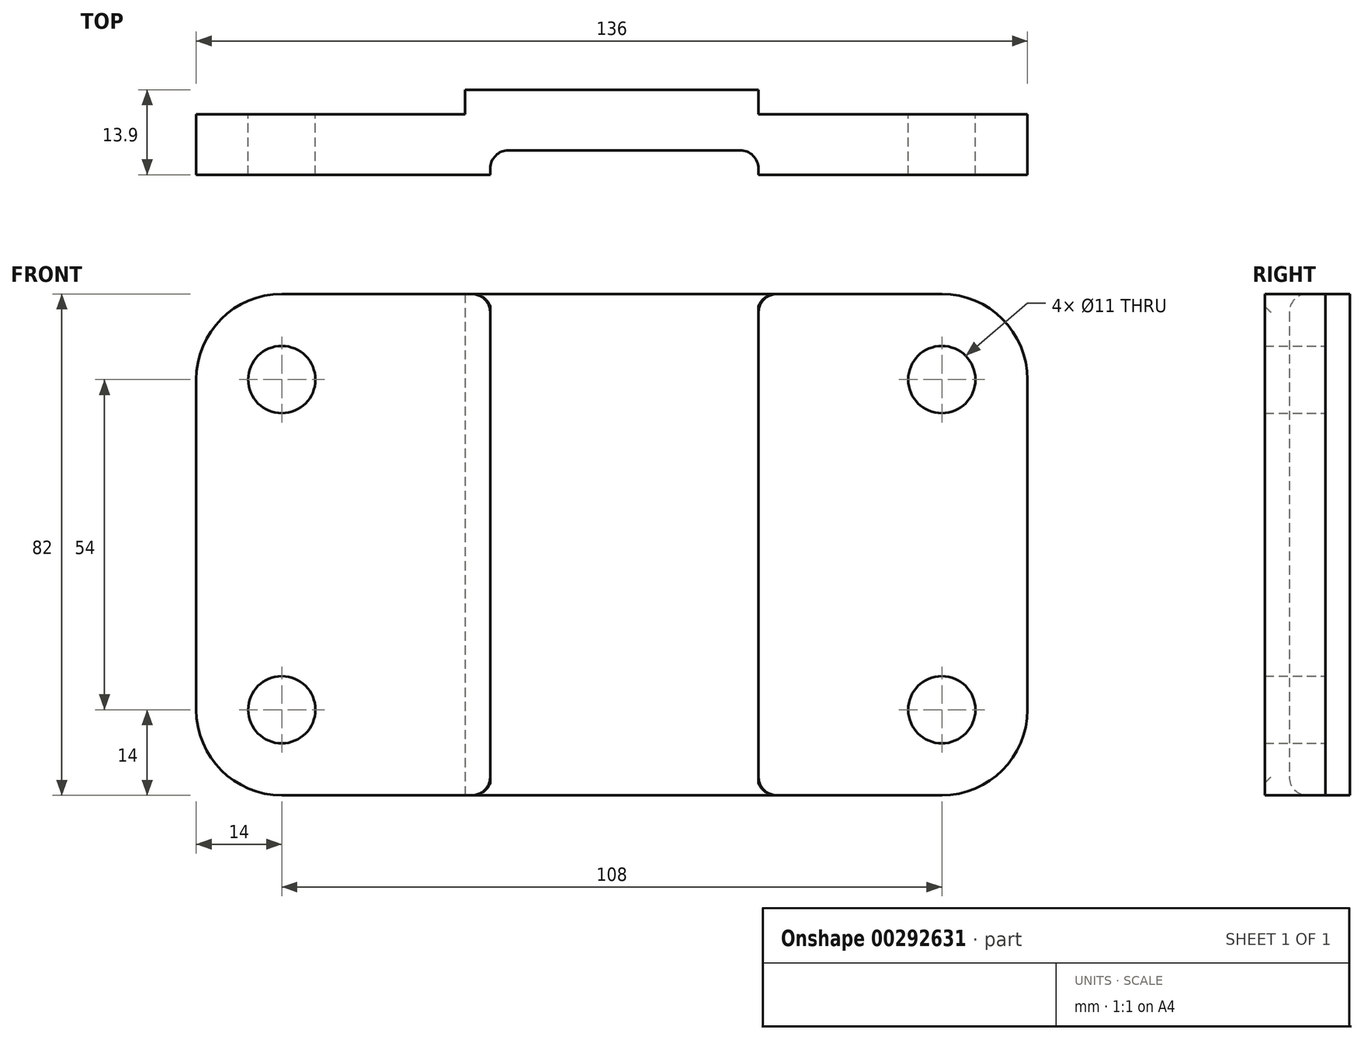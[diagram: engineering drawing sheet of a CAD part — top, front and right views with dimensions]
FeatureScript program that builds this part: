
annotation { "Feature Type Name" : "Feature", "Feature Type Description" : "" }
export const myFeature = defineFeature(function(context is Context, id is Id, definition is map)
    precondition{}
    {
        {
            var Q0;
            Q0=qCreatedBy(makeId("Front.planeOp"),FACE);
            var sketch = newSketch(context, id + "F0", { "sketchPlane" : qUnion([Q0])});
            skLineSegment(sketch, "E0.bottom", {"start": v(14, 0) * mm, "end": v(122, 0) * mm});
            skLineSegment(sketch, "E0.top", {"start": v(14, 82) * mm, "end": v(122, 82) * mm});
            skLineSegment(sketch, "E0.left", {"start": v(0, 14) * mm, "end": v(0, 68) * mm});
            skLineSegment(sketch, "E0.right", {"start": v(136, 14) * mm, "end": v(136, 68) * mm});
            skPoint(sketch, "E1.visualSharp", {"position": v(0, 82) * mm});
            skArc(sketch, "E1.filletArc", {"start": v(14, 82) * mm, "mid": v(4.1, 77.9) * mm, "end": v(0, 68) * mm});
            skPoint(sketch, "E2.visualSharp", {"position": v(136, 82) * mm});
            skArc(sketch, "E2.filletArc", {"start": v(136, 68) * mm, "mid": v(131.9, 77.9) * mm, "end": v(122, 82) * mm});
            skPoint(sketch, "E3.visualSharp", {"position": v(136, 0) * mm});
            skArc(sketch, "E3.filletArc", {"start": v(122, 0) * mm, "mid": v(131.9, 4.1) * mm, "end": v(136, 14) * mm});
            skPoint(sketch, "E4.visualSharp", {"position": v(0, 0) * mm});
            skArc(sketch, "E4.filletArc", {"start": v(0, 14) * mm, "mid": v(4.1, 4.1) * mm, "end": v(14, 0) * mm});
            skCircle(sketch, "E5", {"center": v(14, 68) * mm, "radius": 5.5 * mm});
            skCircle(sketch, "E6", {"center": v(14, 14) * mm, "radius": 5.5 * mm});
            skCircle(sketch, "E7", {"center": v(122, 68) * mm, "radius": 5.5 * mm});
            skCircle(sketch, "E8", {"center": v(122, 14) * mm, "radius": 5.5 * mm});
            skPoint(sketch, "E9", {"position": v(44, 82) * mm});
            skPoint(sketch, "E10", {"position": v(92, 82) * mm});
            skLineSegment(sketch, "E11", {"start": v(44, 82) * mm, "end": v(44, 0) * mm});
            skLineSegment(sketch, "E12", {"start": v(92, 82) * mm, "end": v(92, 0) * mm});
            skSolve(sketch);
        }
        {
            var Q0;
            {var subQ0=sQuery(id+"F0.wireOp",EDGE,"E11");Q0=makeQuery(id+"F0.imprint","IMPRINT",FACE,{"disambiguationData":[TD([[makeQuery(id+"F0.imprint","IMPRINT",EDGE,{"derivedFrom":subQ0}),1.0]])]});}
            extrude(context, id + "F1", {"entities" : qUnion([Q0]), "oppositeDirection" : true, "depth" : 4 * mm});
        }
        {
            var Q0;
            Q0 = qSketchRegion(id + "F0", true);
            extrude(context, id + "F2", {"entities" : qUnion([Q0]), "operationType" : NewBodyOperationType.ADD, "depth" : 9.9 * mm});
        }
        {
            var Q0;
            Q0=makeQuery(id+"F2.opExtrude","CAP_FACE",FACE,{"disambiguationData":[OSD([sQuery(id+"F0.wireOp",EDGE,"E0.bottom"),sQuery(id+"F0.wireOp",EDGE,"E0.top"),sQuery(id+"F0.wireOp",EDGE,"E0.left"),sQuery(id+"F0.wireOp",EDGE,"E0.right"),sQuery(id+"F0.wireOp",EDGE,"E1.filletArc"),sQuery(id+"F0.wireOp",EDGE,"E2.filletArc"),sQuery(id+"F0.wireOp",EDGE,"E3.filletArc"),sQuery(id+"F0.wireOp",EDGE,"E4.filletArc"),sQuery(id+"F0.wireOp",EDGE,"E5"),sQuery(id+"F0.wireOp",EDGE,"E6"),sQuery(id+"F0.wireOp",EDGE,"E7"),sQuery(id+"F0.wireOp",EDGE,"E8")])],"isStart":false});
            var sketch = newSketch(context, id + "F3", { "sketchPlane" : qUnion([Q0])});
            skPoint(sketch, "E13", {"position": v(48.1, 82) * mm});
            skPoint(sketch, "E14", {"position": v(92, 82) * mm});
            skLineSegment(sketch, "E15", {"start": v(48.1, 82) * mm, "end": v(48.1, 0) * mm});
            skLineSegment(sketch, "E16", {"start": v(92, 82) * mm, "end": v(92, 0) * mm});
            skSolve(sketch);
        }
        {
            var Q0;
            {var subQ0=sQuery(id+"F3.wireOp",EDGE,"E15");Q0=makeQuery(id+"F3.imprint","IMPRINT",FACE,{"disambiguationData":[TD([[makeQuery(id+"F3.imprint","IMPRINT",EDGE,{"derivedFrom":subQ0}),1.0]])]});}
            extrude(context, id + "F4", {"entities" : qUnion([Q0]), "operationType" : NewBodyOperationType.REMOVE, "oppositeDirection" : true, "depth" : 4 * mm});
        }
        {
            var Q0;
            Q0=makeQuery(id+"F4.boolean.opBoolean","COPY",EDGE,{"derivedFrom":makeQuery(id+"F4.opExtrude","CAP_EDGE",EDGE,{"disambiguationData":[OSD([sQuery(id+"F3.wireOp",EDGE,"E15")])],"isStart":false})});
            var Q1;
            Q1=makeQuery(id+"F4.boolean.opBoolean","COPY",FACE,{"derivedFrom":makeQuery(id+"F4.opExtrude","CAP_FACE",FACE,{"disambiguationData":[OSD([sQuery(id+"F0.wireOp",EDGE,"E0.bottom"),sQuery(id+"F0.wireOp",EDGE,"E0.top"),sQuery(id+"F3.wireOp",EDGE,"E15"),sQuery(id+"F3.wireOp",EDGE,"E16")])],"isStart":false})});
            fillet(context, id + "F5", {"entities" : qUnion([Q0, Q1]), "radius" : 3 * mm, "tangentPropagation" : true, "allowEdgeOverflow" : false});
        }
    });
